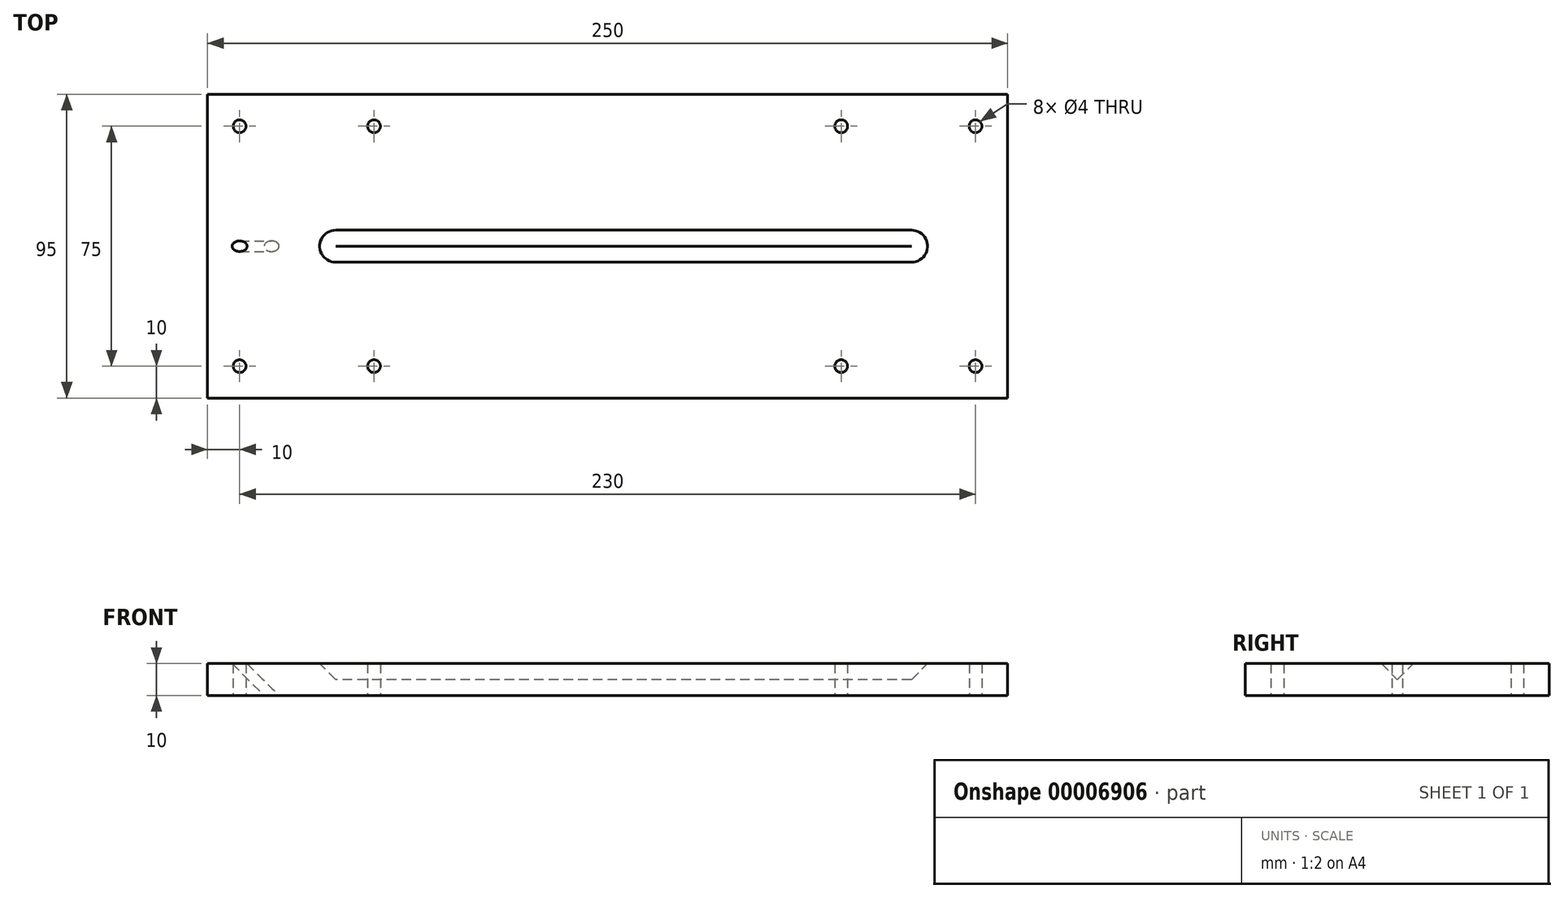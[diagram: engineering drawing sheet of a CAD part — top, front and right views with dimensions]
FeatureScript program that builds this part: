
annotation { "Feature Type Name" : "Feature", "Feature Type Description" : "" }
export const myFeature = defineFeature(function(context is Context, id is Id, definition is map)
    precondition{}
    {
        {
            var Q0;
            Q0=qCreatedBy(makeId("Top.planeOp"),FACE);
            var sketch = newSketch(context, id + "F0", { "sketchPlane" : qUnion([Q0])});
            skLineSegment(sketch, "E0.rect.bottom", {"start": v(125, -47.5) * mm, "end": v(-125, -47.5) * mm});
            skLineSegment(sketch, "E0.rect.top", {"start": v(125, 47.5) * mm, "end": v(-125, 47.5) * mm});
            skLineSegment(sketch, "E0.rect.left", {"start": v(125, -47.5) * mm, "end": v(125, 47.5) * mm});
            skLineSegment(sketch, "E0.rect.right", {"start": v(-125, -47.5) * mm, "end": v(-125, 47.5) * mm});
            skPoint(sketch, "E0.rect.middle", {"position": v(0, 0) * mm});
            skLineSegment(sketch, "E1", {"start": v(-125, 0) * mm, "end": v(125, 0) * mm, "construction": true});
            skLineSegment(sketch, "E2", {"start": v(-86.5, 47.5) * mm, "end": v(-86.5, -47.5) * mm, "construction": true});
            skLineSegment(sketch, "E3", {"start": v(-48.5, 47.5) * mm, "end": v(-48.5, -47.5) * mm, "construction": true});
            skLineSegment(sketch, "E4", {"start": v(-10.5, 47.5) * mm, "end": v(-10.5, -47.5) * mm, "construction": true});
            skCircle(sketch, "E5", {"center": v(-115, 37.5) * mm, "radius": 2 * mm});
            skCircle(sketch, "E6", {"center": v(-73, 37.5) * mm, "radius": 2 * mm});
            skCircle(sketch, "E7", {"center": v(73, 37.5) * mm, "radius": 2 * mm});
            skCircle(sketch, "E8", {"center": v(115, 37.5) * mm, "radius": 2 * mm});
            skCircle(sketch, "E9", {"center": v(115, -37.5) * mm, "radius": 2 * mm});
            skCircle(sketch, "E10", {"center": v(73, -37.5) * mm, "radius": 2 * mm});
            skCircle(sketch, "E11", {"center": v(-73, -37.5) * mm, "radius": 2 * mm});
            skCircle(sketch, "E12", {"center": v(-115, -37.5) * mm, "radius": 2 * mm});
            skSolve(sketch);
        }
        {
            var Q0;
            Q0=qSketchRegion(id+"F0",true);
            var Q1;
            Q1=makeQuery(id+"F0.imprint","IMPRINT",FACE,{"disambiguationData":[TD([[makeQuery(id+"F0.imprint","IMPRINT",EDGE,{"derivedFrom":sQuery(id+"F0.wireOp",EDGE,"E0.rect.bottom")}),-1.0]])]});
            extrude(context, id + "F1", {"entities" : qUnion([Q0, Q1]), "depth" : (10) * mm});
        }
        {
            var Q0;
            Q0=makeQuery(id+"F1.opExtrude","SWEPT_FACE",FACE,{"disambiguationData":[OSD([sQuery(id+"F0.wireOp",EDGE,"E0.rect.right")])]});
            var sketch = newSketch(context, id + "F2", { "sketchPlane" : qUnion([Q0])});
            skLineSegment(sketch, "E13", {"start": v(0, 10) * mm, "end": v(0, 0) * mm, "construction": true});
            skLineSegment(sketch, "E14", {"start": v(5, 10) * mm, "end": v(0, 5) * mm});
            skLineSegment(sketch, "E15", {"start": v(0, 5) * mm, "end": v(-5, 10) * mm});
            skSolve(sketch);
        }
        {
            var Q0;
            {var subQ2=sQuery(id+"F2.wireOp",EDGE,"E14");Q0=makeQuery(id+"F2.imprint","IMPRINT",FACE,{"disambiguationData":[TD([[makeQuery(id+"F2.imprint","IMPRINT",EDGE,{"derivedFrom":subQ2}),-1.0]])]});}
            extrude(context, id + "F3", {"entities" : qUnion([Q0]), "operationType" : NewBodyOperationType.REMOVE, "oppositeDirection" : true, "depth" : (220) * mm});
        }
        {
            var Q0;
            Q0=makeQuery(id+"F3.boolean.opBoolean","COPY",FACE,{"derivedFrom":makeQuery(id+"F3.opExtrude","CAP_FACE",FACE,{"disambiguationData":[OSD([sQuery(id+"F0.wireOp",EDGE,"E0.rect.right"),sQuery(id+"F2.wireOp",EDGE,"E14"),sQuery(id+"F2.wireOp",EDGE,"E15")])],"isStart":false})});
            var sketch = newSketch(context, id + "F4", { "sketchPlane" : qUnion([Q0])});
            skLineSegment(sketch, "E16", {"start": v(0, 5) * mm, "end": v(0, 10) * mm});
            skSolve(sketch);
        }
        {
            var Q0;
            {var subQ1=sQuery(id+"F4.wireOp",EDGE,"E16");Q0=makeQuery(id+"F4.imprint","IMPRINT",FACE,{"disambiguationData":[TD([[makeQuery(id+"F4.imprint","IMPRINT",EDGE,{"derivedFrom":subQ1}),-1.0]])]});}
            var Q1;
            Q1=sQuery(id+"F4.wireOp",EDGE,"E16");
            revolve(context, id + "F5", {"operationType" : NewBodyOperationType.REMOVE, "entities" : qUnion([Q0]), "axis" : qUnion([Q1]), "revolveType" : RevolveType.FULL, "oppositeDirection" : true});
        }
        {
            var Q0;
            Q0=makeQuery(id+"F1.opExtrude","SWEPT_FACE",FACE,{"disambiguationData":[OSD([sQuery(id+"F0.wireOp",EDGE,"E0.rect.right")])]});
            var sketch = newSketch(context, id + "F6", { "sketchPlane" : qUnion([Q0])});
            skLineSegment(sketch, "E17", {"start": v(-5, 10) * mm, "end": v(5, 10) * mm});
            skSolve(sketch);
        }
        {
            var Q0;
            Q0 = qSketchRegion(id + "F6", true);
            var Q1;
            Q1=makeQuery(id+"F6.imprint","IMPRINT",FACE,{"disambiguationData":[TD([[makeQuery(id+"F6.imprint","IMPRINT",EDGE,{"derivedFrom":sQuery(id+"F6.wireOp",EDGE,"E17")}),-1.0]])]});
            extrude(context, id + "F7", {"entities" : qUnion([Q0, Q1]), "operationType" : NewBodyOperationType.ADD, "oppositeDirection" : true, "depth" : 40 * mm});
        }
        {
            var Q0;
            Q0=makeQuery(id+"F7.opExtrude","CAP_FACE",FACE,{"disambiguationData":[OSD([sQuery(id+"F2.wireOp",EDGE,"E14"),sQuery(id+"F2.wireOp",EDGE,"E15"),sQuery(id+"F6.wireOp",EDGE,"E17")])],"isStart":false});
            var sketch = newSketch(context, id + "F8", { "sketchPlane" : qUnion([Q0])});
            skLineSegment(sketch, "E18", {"start": v(0, 5) * mm, "end": v(0, 10) * mm});
            skSolve(sketch);
        }
        {
            var Q0;
            Q0 = qSketchRegion(id + "F8", true);
            var Q1;
            {var subQ1=sQuery(id+"F8.wireOp",EDGE,"E18");Q1=makeQuery(id+"F8.imprint","IMPRINT",FACE,{"disambiguationData":[TD([[makeQuery(id+"F8.imprint","IMPRINT",EDGE,{"derivedFrom":subQ1}),-1.0]])]});}
            var Q2;
            Q2=sQuery(id+"F8.wireOp",EDGE,"E18");
            revolve(context, id + "F9", {"operationType" : NewBodyOperationType.REMOVE, "entities" : qUnion([Q0, Q1]), "axis" : qUnion([Q2]), "revolveType" : RevolveType.FULL, "oppositeDirection" : true});
        }
        {
            var Q0;
            Q0=makeQuery(id+"F7.boolean.opBoolean","MERGE",FACE,{"derivedFrom":[makeQuery(id+"F1.opExtrude","CAP_FACE",FACE,{"disambiguationData":[OSD([sQuery(id+"F0.wireOp",EDGE,"E0.rect.bottom"),sQuery(id+"F0.wireOp",EDGE,"E0.rect.top"),sQuery(id+"F0.wireOp",EDGE,"E0.rect.left"),sQuery(id+"F0.wireOp",EDGE,"E0.rect.right"),sQuery(id+"F0.wireOp",EDGE,"E5"),sQuery(id+"F0.wireOp",EDGE,"E6"),sQuery(id+"F0.wireOp",EDGE,"E7"),sQuery(id+"F0.wireOp",EDGE,"E8"),sQuery(id+"F0.wireOp",EDGE,"E9"),sQuery(id+"F0.wireOp",EDGE,"E10"),sQuery(id+"F0.wireOp",EDGE,"E11"),sQuery(id+"F0.wireOp",EDGE,"E12")])],"isStart":false}),makeQuery(id+"F7.opExtrude","SWEPT_FACE",FACE,{"disambiguationData":[OSD([sQuery(id+"F6.wireOp",EDGE,"E17")])]})]});
            var sketch = newSketch(context, id + "F10", { "sketchPlane" : qUnion([Q0])});
            skLineSegment(sketch, "E19", {"start": v(-125, -47.5) * mm, "end": v(-125, 47.5) * mm, "construction": true});
            skSolve(sketch);
        }
        {
            var Q0;
            Q0=sQuery(id+"F10.wireOp",EDGE,"E19");
            cPlane(context, id + "F11", {"entities" : qUnion([Q0]), "cplaneType" : CPlaneType.LINE_ANGLE, "offset" : 150 * mm, "angle" : 135 * degree, "width" : 150 * mm, "height" : 150 * mm});
        }
        {
            var Q0;
            Q0=qCreatedBy(id+"F11.planeOp",FACE);
            var sketch = newSketch(context, id + "F12", { "sketchPlane" : qUnion([Q0])});
            skCircle(sketch, "E20", {"center": v(0, -74.25) * mm, "radius": 1.65 * mm});
            skSolve(sketch);
        }
        {
            var Q0;
            Q0 = qSketchRegion(id + "F12", true);
            extrude(context, id + "F13", {"entities" : qUnion([Q0]), "operationType" : NewBodyOperationType.REMOVE, "oppositeDirection" : true, "depth" : (50) * mm, "hasSecondDirection" : true, "secondDirectionOppositeDirection" : false, "secondDirectionDepth" : (50) * mm});
        }
    });
